# Revit family: Gira_086100
name_source: partatom
category: Elektroinstallationen
revit_build: Autodesk Revit 2017 (Build: 20160225_1515(x64)
units: mm (PartAtom-declared; Revit-internal decimal feet)

## family parameters
Basisbauteil = Fläche
Beim Laden mit Abzugskörper schneiden = Nein
Bemaßung runder Anschluss = Durchmesser verwenden
Beschriftungsausrichtung beibehalten = Nein
Gemeinsam genutzt = Nein
Raumberechnungspunkt = Nein
Teiletyp = Normal

## types (1)
- Trennrelais 2f REG Jalousie
    Anzahl der anschließbaren Motoren = 2
    BIM = https://media.live.bim.site 00_REG 2.5.rfa
    BIMSITE_PRODUCT_ID = 5451681ee89bcbe04bd01c97bd85773aa633bdb1
    Beschreibung = Trennrelais 2fach  REG Merkmale:  Gleichzeitige Ansteuerung von mehreren Jalousieantrieben.  Je zwei Antriebe werden mit einem Trennrelais elektrisch entkoppelt.  Mit zwei Nebenstelleneingängen für die Einzelbedienung der Jalousien und einem Zentraleingang für Zentralfunktion, z. B. von einer Zeitschaltuhr oder zur Umsetzung von Zentralsteuerungen bei Aufteilung auf mehrere FI-Schutzschalter.  Hinweise :  Das Trennrelais REG wird auf einer Hutprofilschiene montiert.
    Datenblatt = https://media.live.bim.site
    Datenblatt 1 = https://media.live.bim.site
    GTIN = 4010337861003
    HAN = 086100
    HeinzeBIM = https://www.heinze.de
    Hersteller = Gira
    Ist System = Nein
    Ist Zubehör = Nein
    Kosten = 0 $
    Montageart = REG
    Nebenstelleneingang = Ja
    Produktseite = https://media.live.bim.site
    Typname = Trennrelais 2f REG Jalousie
    URL = https://www.gira.de
    Vorgabe-Ansicht = 1219 mm
    Zentraleingang = Nein

## geometry (parser evidence)
native form markers: Sweep x1
no freeform markers — native parametric forms only
